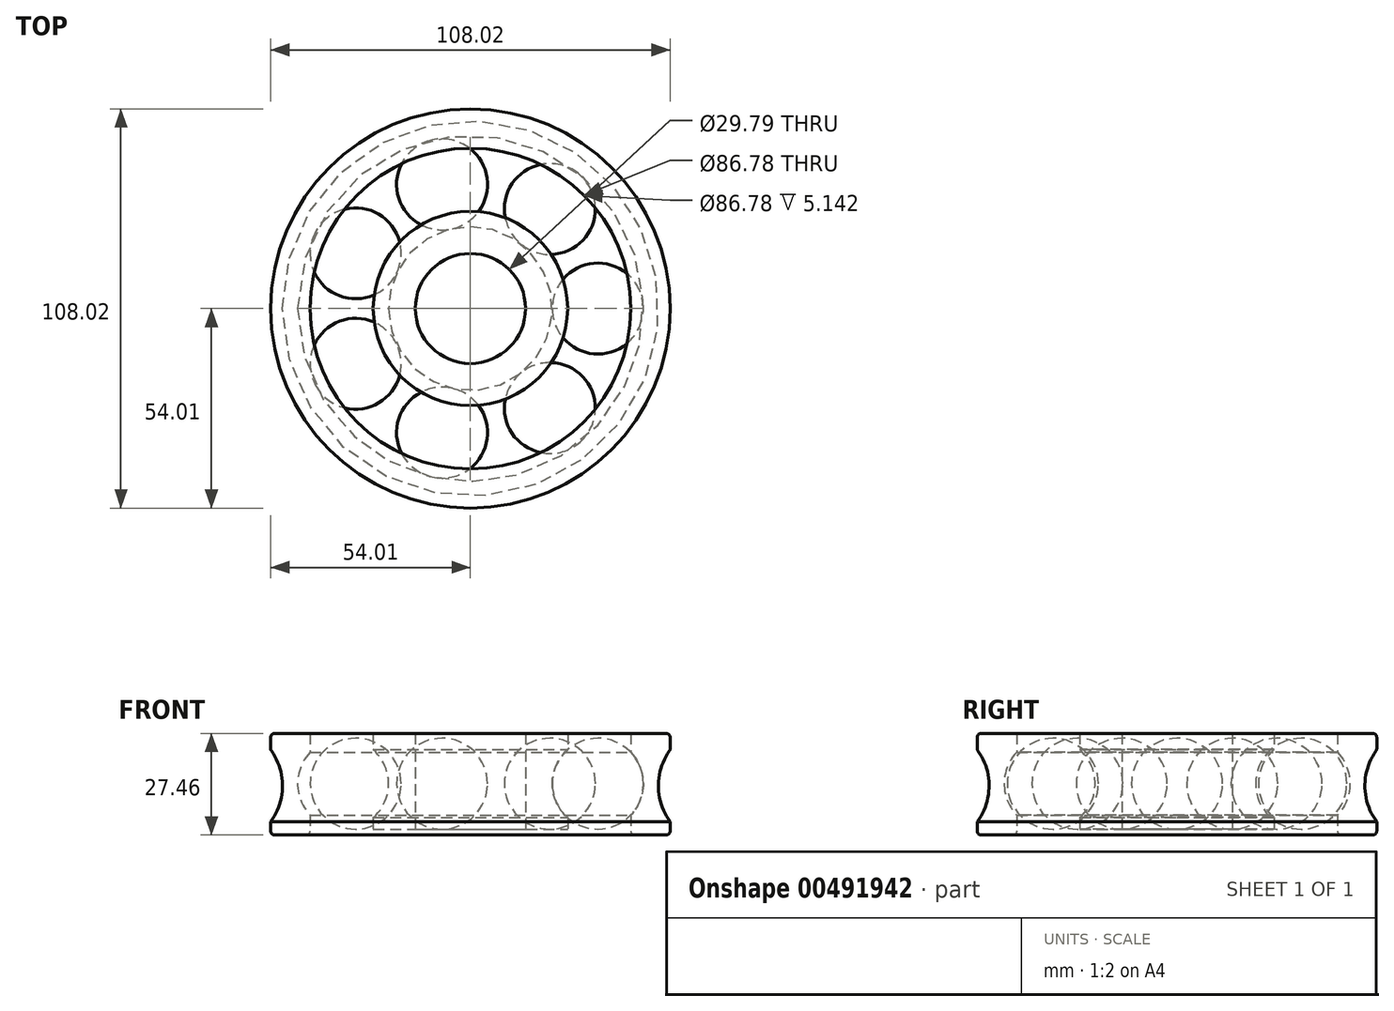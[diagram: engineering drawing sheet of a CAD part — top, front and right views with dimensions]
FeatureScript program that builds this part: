
annotation { "Feature Type Name" : "Feature", "Feature Type Description" : "" }
export const myFeature = defineFeature(function(context is Context, id is Id, definition is map)
    precondition{}
    {
        {
            var Q0;
            Q0=qCreatedBy(makeId("Front.planeOp"),FACE);
            var sketch = newSketch(context, id + "F0", { "sketchPlane" : qUnion([Q0])});
            skLineSegment(sketch, "E0", {"start": v(0, -11.14) * mm, "end": v(0, 13.6) * mm, "construction": true});
            skLineSegment(sketch, "E1.bottom", {"start": v(14.9, 13.6) * mm, "end": v(26.3, 13.6) * mm});
            skLineSegment(sketch, "E1.top", {"start": v(14.9, -12.3) * mm, "end": v(26.3, -12.3) * mm});
            skLineSegment(sketch, "E1.left", {"start": v(14.9, 13.6) * mm, "end": v(14.9, -12.3) * mm});
            skLineSegment(sketch, "E1.right", {"start": v(26.3, 13.6) * mm, "end": v(26.3, 9.2) * mm});
            skLineSegment(sketch, "E2", {"start": v(14.9, 0) * mm, "end": v(22.15, 0) * mm, "construction": true});
            skLineSegment(sketch, "E3.bottom", {"start": v(43.4, 13.6) * mm, "end": v(54.01, 13.6) * mm});
            skLineSegment(sketch, "E3.top", {"start": v(43.4, -13.86) * mm, "end": v(54.01, -13.86) * mm});
            skLineSegment(sketch, "E3.left", {"start": v(43.4, 13.6) * mm, "end": v(43.4, 8.46) * mm});
            skLineSegment(sketch, "E3.right", {"start": v(54.01, 13.6) * mm, "end": v(54.01, 9.12) * mm});
            skLineSegment(sketch, "E4", {"start": v(22.15, 0) * mm, "end": v(46.76, 0) * mm});
            skLineSegment(sketch, "E5", {"start": v(46.76, 0) * mm, "end": v(54.01, 0) * mm, "construction": true});
            skCircle(sketch, "E6", {"center": v(34.45, 0) * mm, "radius": 12.3 * mm});
            skLineSegment(sketch, "E7", {"start": v(26.3, 9.2) * mm, "end": v(26.3, -9.2) * mm});
            skLineSegment(sketch, "E8", {"start": v(26.3, -9.2) * mm, "end": v(26.3, -12.3) * mm});
            skLineSegment(sketch, "E9", {"start": v(43.4, -8.46) * mm, "end": v(43.4, -13.86) * mm});
            skLineSegment(sketch, "E10", {"start": v(43.4, 8.46) * mm, "end": v(43.4, -8.46) * mm});
            skArc(sketch, "E11", {"start": v(54.01, 9.12) * mm, "mid": v(50.82, -0.57) * mm, "end": v(54.01, -10.26) * mm});
            skLineSegment(sketch, "E12", {"start": v(54.01, -10.26) * mm, "end": v(54.01, -13.86) * mm});
            skLineSegment(sketch, "E13", {"start": v(54.01, 9.12) * mm, "end": v(54.01, -10.26) * mm, "construction": true});
            skSolve(sketch);
        }
        {
            var Q0;
            {var subQ1=sQuery(id+"F0.wireOp",EDGE,"E1.bottom");Q0=makeQuery(id+"F0.imprint","IMPRINT",FACE,{"disambiguationData":[TD([[makeQuery(id+"F0.imprint","IMPRINT",EDGE,{"derivedFrom":subQ1}),-1.0]])]});}
            var Q1;
            {var subQ1=sQuery(id+"F0.wireOp",EDGE,"E3.bottom");Q1=makeQuery(id+"F0.imprint","IMPRINT",FACE,{"disambiguationData":[TD([[makeQuery(id+"F0.imprint","IMPRINT",EDGE,{"derivedFrom":subQ1}),-1.0]])]});}
            var Q2;
            Q2=sQuery(id+"F0.wireOp",EDGE,"E0");
            revolve(context, id + "F1", {"entities" : qUnion([Q0, Q1]), "axis" : qUnion([Q2]), "revolveType" : RevolveType.FULL});
        }
        {
            var Q0;
            {var subQ0=sQuery(id+"F0.wireOp",EDGE,"E7");var subQ1=sQuery(id+"F0.wireOp",EDGE,"E4");var subQ2=makeQuery(id+"F0.imprint","INTERSECT",VERTEX,{"derivedFrom":[subQ1,subQ0]});Q0=makeQuery(id+"F0.imprint","IMPRINT",FACE,{"disambiguationData":[TD([[makeQuery(id+"F0.imprint","IMPRINT",EDGE,{"disambiguationData":[TD([[subQ2,-1.0]])],"derivedFrom":subQ1}),1.0]])]});}
            var Q1;
            {var subQ0=sQuery(id+"F0.wireOp",EDGE,"E6");var subQ1=sQuery(id+"F0.wireOp",EDGE,"E4");var subQ2=makeQuery(id+"F0.imprint","INTERSECT",VERTEX,{"disambiguationData":[OD(0.0)],"derivedFrom":[subQ1,subQ0]});Q1=makeQuery(id+"F0.imprint","IMPRINT",FACE,{"disambiguationData":[TD([[makeQuery(id+"F0.imprint","IMPRINT",EDGE,{"disambiguationData":[TD([[subQ2,-1.0]])],"derivedFrom":subQ1}),1.0]])]});}
            var Q2;
            {var subQ0=sQuery(id+"F0.wireOp",EDGE,"E6");var subQ1=sQuery(id+"F0.wireOp",EDGE,"E4");var subQ2=makeQuery(id+"F0.imprint","INTERSECT",VERTEX,{"disambiguationData":[OD(1.0)],"derivedFrom":[subQ1,subQ0]});Q2=makeQuery(id+"F0.imprint","IMPRINT",FACE,{"disambiguationData":[TD([[makeQuery(id+"F0.imprint","IMPRINT",EDGE,{"disambiguationData":[TD([[subQ2,1.0]])],"derivedFrom":subQ1}),1.0]])]});}
            var Q3;
            Q3=sQuery(id+"F0.wireOp",EDGE,"E4");
            revolve(context, id + "F2", {"entities" : qUnion([Q0, Q1, Q2]), "axis" : qUnion([Q3]), "revolveType" : RevolveType.FULL});
        }
        {
            var Q0;
            Q0=makeQuery(id+"F2.opRevolve","SWEPT_BODY",BODY,{"disambiguationData":[OSD([sQuery(id+"F0.wireOp",EDGE,"E4"),sQuery(id+"F0.wireOp",EDGE,"E6")])]});
            var Q1;
            Q1=sQuery(id+"F0.wireOp",EDGE,"E0");
            circularPattern(context, id + "F3", {"entities" : qUnion([Q0]), "axis" : qUnion([Q1]), "angle" : 360 * degree, "instanceCount" : 7, "equalSpace" : true});
        }
        {
            var Q0;
            Q0=makeQuery(id+"F1.opRevolve","SWEPT_EDGE",EDGE,{"disambiguationData":[OSD([sQuery(id+"F0.wireOp",EDGE,"E3.bottom"),sQuery(id+"F0.wireOp",EDGE,"E3.right")])]});
            var Q1;
            Q1=makeQuery(id+"F1.opRevolve","SWEPT_EDGE",EDGE,{"disambiguationData":[OSD([sQuery(id+"F0.wireOp",EDGE,"E3.top"),sQuery(id+"F0.wireOp",EDGE,"E3.right")])]});
            fillet(context, id + "F4", {"entities" : qUnion([Q0, Q1]), "radius" : 1 * mm, "tangentPropagation" : true, "allowEdgeOverflow" : false});
        }
    });
